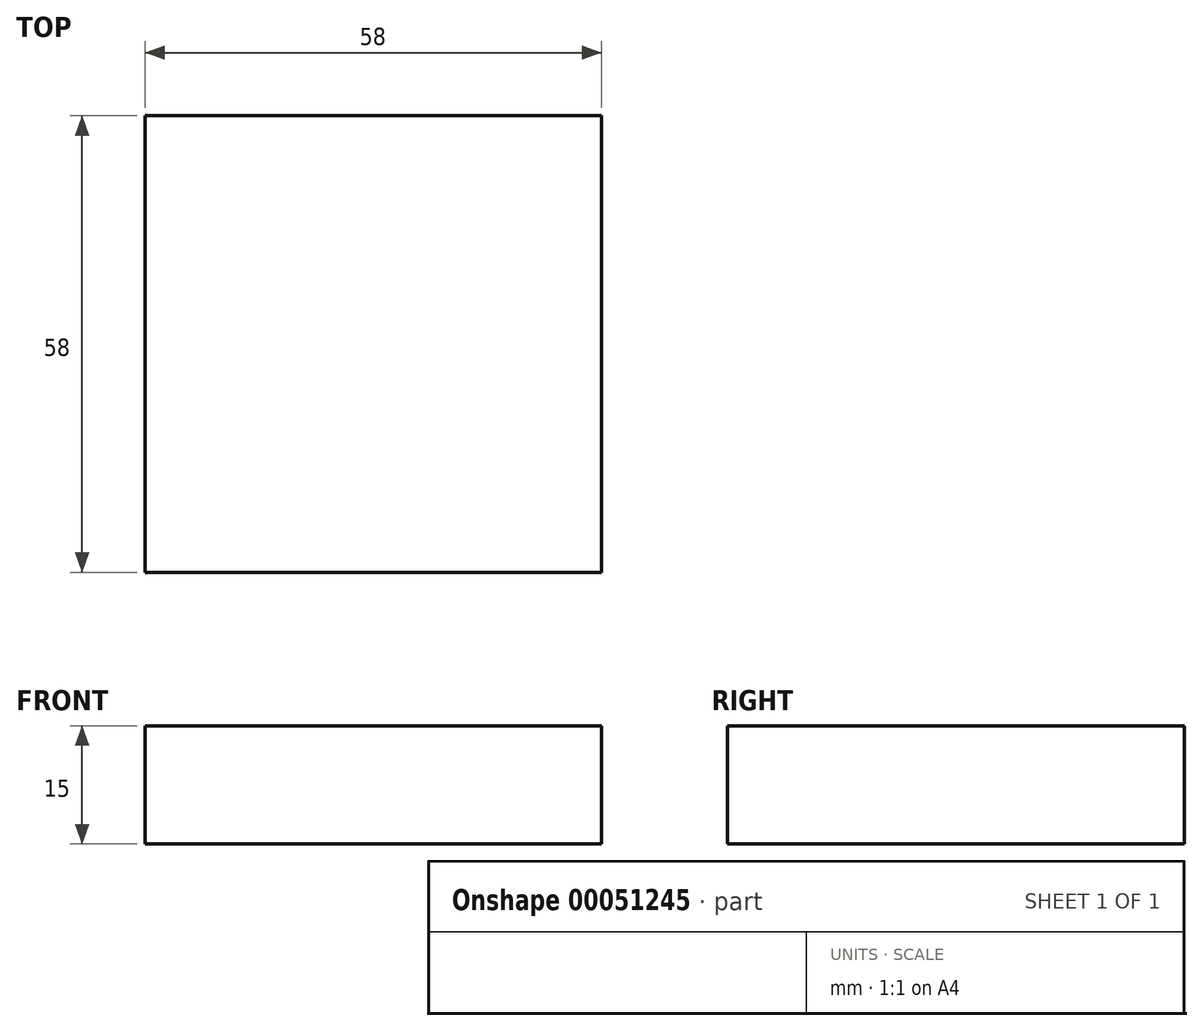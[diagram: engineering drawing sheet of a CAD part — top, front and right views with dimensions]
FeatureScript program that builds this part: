
annotation { "Feature Type Name" : "Feature", "Feature Type Description" : "" }
export const myFeature = defineFeature(function(context is Context, id is Id, definition is map)
    precondition{}
    {
        {
            var Q0;
            Q0=qCreatedBy(makeId("Top.planeOp"),FACE);
            var sketch = newSketch(context, id + "F0", { "sketchPlane" : qUnion([Q0])});
            skLineSegment(sketch, "E0.bottom", {"start": v(0, 0) * mm, "end": v(58, 0) * mm});
            skLineSegment(sketch, "E0.top", {"start": v(0, -58) * mm, "end": v(58, -58) * mm});
            skLineSegment(sketch, "E0.left", {"start": v(0, 0) * mm, "end": v(0, -58) * mm});
            skLineSegment(sketch, "E0.right", {"start": v(58, 0) * mm, "end": v(58, -58) * mm});
            skSolve(sketch);
        }
        {
            var Q0;
            Q0=makeQuery(id+"F0.imprint","IMPRINT",FACE,{"disambiguationData":[TD([[makeQuery(id+"F0.imprint","IMPRINT",EDGE,{"derivedFrom":sQuery(id+"F0.wireOp",EDGE,"E0.bottom")}),-1.0]])]});
            extrude(context, id + "F1", {"entities" : qUnion([Q0]), "depth" : 15 * mm});
        }
    });
